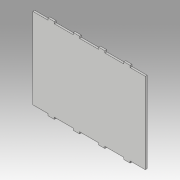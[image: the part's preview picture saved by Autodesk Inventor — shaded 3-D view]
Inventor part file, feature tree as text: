
AUTODESK INVENTOR PART (.ipt)
format: ipt  version: 2019.3 (Build 233278000, 278)  size: 121,344 bytes
history: native  units: mm
features: extrude x1, sketch x1
ambient origin geometry x8: Origin, YZ Plane, XZ Plane, XY Plane, X Axis, Y Axis, Z Axis, Center Point
bodies: Solid1 (feature_tree)
feature tree (2):
  extrude  "Extrusion1"  Depth=30.0mm
  sketch  "Sketch1"  dims[d2=128.0mm d8=30.0mm d9=30.0mm d10=24.0mm d11=30.0mm d12=24.0mm d13=128.0mm d14=178.0mm d15=10.0mm d16=3.0mm d17=3.0mm d18=0.0mm]
